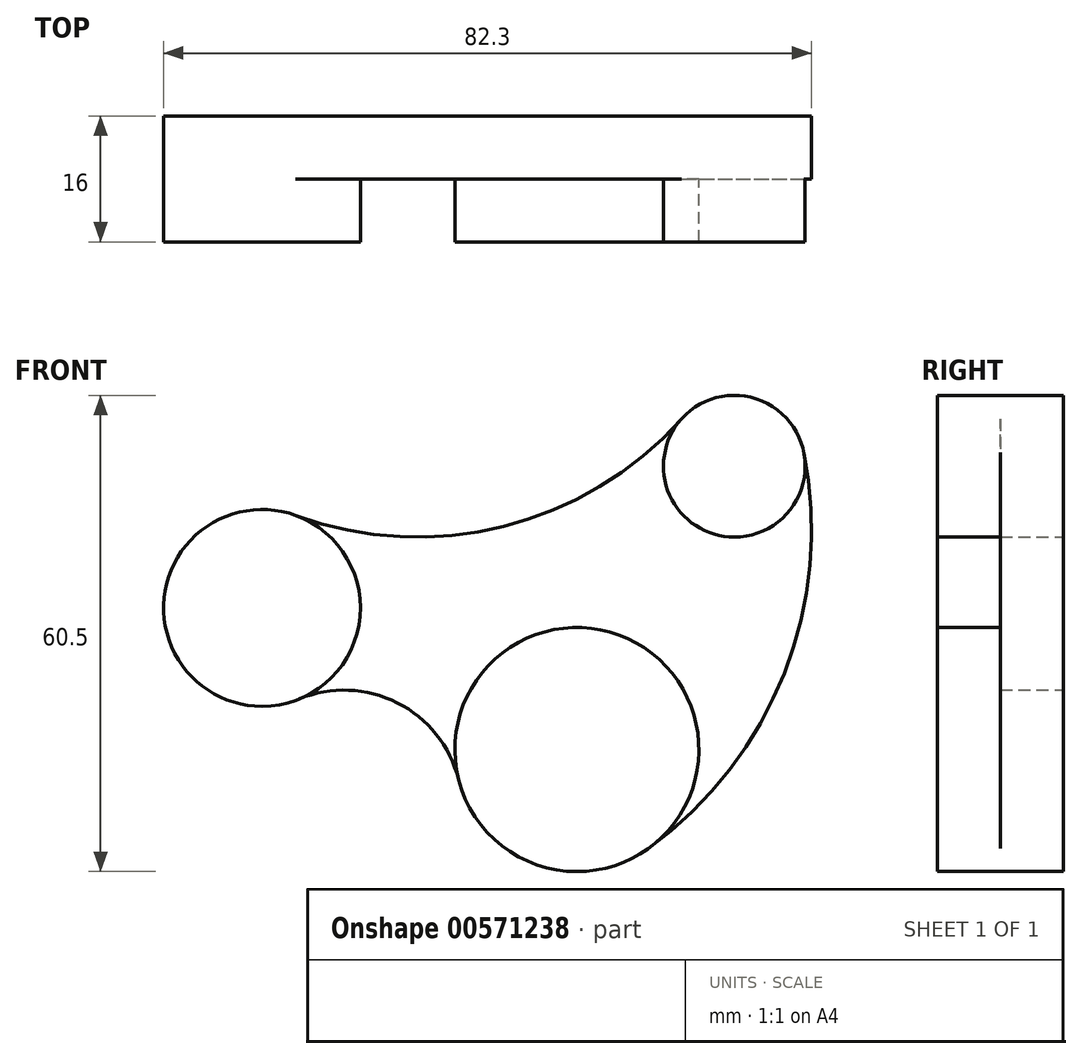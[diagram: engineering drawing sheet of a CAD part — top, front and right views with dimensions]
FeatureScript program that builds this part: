
annotation { "Feature Type Name" : "Feature", "Feature Type Description" : "" }
export const myFeature = defineFeature(function(context is Context, id is Id, definition is map)
    precondition{}
    {
        {
            var Q0;
            Q0=qCreatedBy(makeId("Front.planeOp"),FACE);
            var sketch = newSketch(context, id + "F0", { "sketchPlane" : qUnion([Q0])});
            skCircle(sketch, "E0", {"center": v(0, 0) * mm, "radius": 15.5 * mm});
            skCircle(sketch, "E1", {"center": v(-40, 18) * mm, "radius": 12.5 * mm});
            skCircle(sketch, "E2", {"center": v(20, 36) * mm, "radius": 9 * mm});
            skArc(sketch, "E3", {"start": v(9.08, -12.56) * mm, "mid": v(26.34, 9.7) * mm, "end": v(28.83, 37.76) * mm});
            skArc(sketch, "E4", {"start": v(-15.03, -3.79) * mm, "mid": v(-22.81, 5.94) * mm, "end": v(-35.26, 6.43) * mm});
            skArc(sketch, "E5", {"start": v(-35.7, 29.74) * mm, "mid": v(-9.32, 28.35) * mm, "end": v(13.3, 42) * mm});
            skSolve(sketch);
        }
        {
            var Q0;
            {var subQ0=sQuery(id+"F0.wireOp",EDGE,"E3");Q0=makeQuery(id+"F0.imprint","IMPRINT",FACE,{"disambiguationData":[TD([[makeQuery(id+"F0.imprint","IMPRINT",EDGE,{"derivedFrom":subQ0}),1.0]])]});}
            extrude(context, id + "F1", {"entities" : qUnion([Q0]), "depth" : 8 * mm, "offsetDistance" : 25 * mm});
        }
        {
            var Q0;
            {var subQ0=sQuery(id+"F0.wireOp",EDGE,"E1");var subQ1=makeQuery(id+"F0.imprint","INTERSECT",VERTEX,{"derivedFrom":[subQ0,sQuery(id+"F0.wireOp",EDGE,"E4")]});Q0=makeQuery(id+"F0.imprint","IMPRINT",FACE,{"disambiguationData":[TD([[makeQuery(id+"F0.imprint","IMPRINT",EDGE,{"disambiguationData":[TD([[subQ1,1.0]])],"derivedFrom":subQ0}),1.0]])]});}
            var Q1;
            {var subQ0=sQuery(id+"F0.wireOp",EDGE,"E0");var subQ1=makeQuery(id+"F0.imprint","INTERSECT",VERTEX,{"derivedFrom":[subQ0,sQuery(id+"F0.wireOp",EDGE,"E3")]});Q1=makeQuery(id+"F0.imprint","IMPRINT",FACE,{"disambiguationData":[TD([[makeQuery(id+"F0.imprint","IMPRINT",EDGE,{"disambiguationData":[TD([[subQ1,1.0]])],"derivedFrom":subQ0}),1.0]])]});}
            var Q2;
            {var subQ0=sQuery(id+"F0.wireOp",EDGE,"E2");var subQ1=makeQuery(id+"F0.imprint","INTERSECT",VERTEX,{"derivedFrom":[subQ0,sQuery(id+"F0.wireOp",EDGE,"E3")]});Q2=makeQuery(id+"F0.imprint","IMPRINT",FACE,{"disambiguationData":[TD([[makeQuery(id+"F0.imprint","IMPRINT",EDGE,{"disambiguationData":[TD([[subQ1,-1.0]])],"derivedFrom":subQ0}),1.0]])]});}
            extrude(context, id + "F2", {"entities" : qUnion([Q0, Q1, Q2]), "operationType" : NewBodyOperationType.ADD, "depth" : 16 * mm, "offsetDistance" : 25 * mm});
        }
    });
